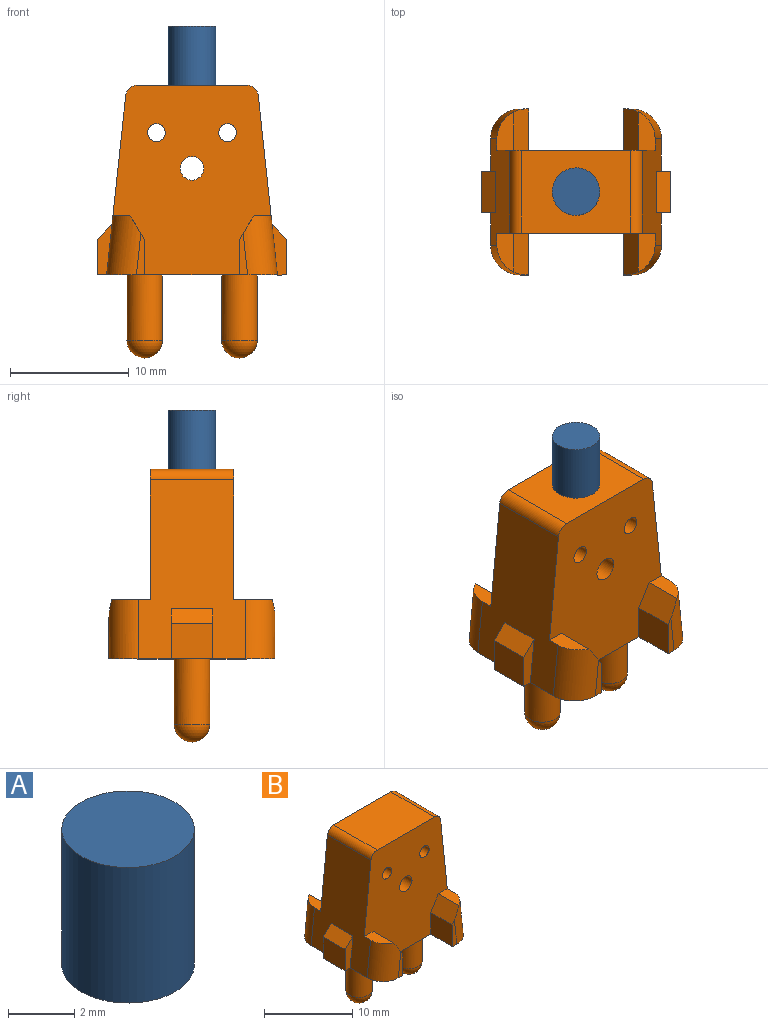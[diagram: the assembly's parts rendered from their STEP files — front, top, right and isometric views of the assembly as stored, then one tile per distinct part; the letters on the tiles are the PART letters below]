
ASSEMBLY  parts=2 mates=1
PART A: 3 faces, bbox 4x4x5 mm
  f0: cylinder r=2mm len=5mm, axis (0,0,-1), area 62.8mm2, adj f1,f2
  f1: plane 4x4mm, normal (0,0,1), area 12.6mm2, adj f0
  f2: plane 4x4mm, normal (0,0,-1), area 12.6mm2, adj f0
PART B: 43 faces, bbox 16x14x23 mm
  f0: plane 15.11x9mm, normal (0.99,0,0.11), area 101.4mm2, adj f1,f7,f9,f10,f22,f24,f32,f34
  f1: cylinder r=1mm len=7mm, axis (0,1,0), area 10.3mm2, adj f0,f2,f9,f10
  f2: plane 9.2x7mm, normal (0,0,1), area 64.4mm2, adj f1,f3,f9,f10
  f3: cylinder r=1mm len=7mm, axis (0,1,0), area 10.3mm2, adj f2,f4,f9,f10
  f4: plane 15.11x9mm, normal (-0.99,0,0.11), area 101.4mm2, adj f3,f7,f9,f10,f17,f19,f27,f29
  f5: cylinder r=1mm len=7mm, axis (0,1,0), area 44mm2, adj f9,f10
  f6: cylinder r=0.75mm len=7mm, axis (0,1,0), area 33mm2, adj f9,f10
  f7: plane 16x14mm, normal (0,0,-1), area 131.7mm2, adj f0,f4,f9,f10,f11,f12,f15,f18
  f8: cylinder r=0.75mm len=7mm, axis (0,1,0), area 33mm2, adj f9,f10
  f9: plane 16x13.34mm, normal (0,-1,0), area 169.3mm2, adj f0,f1,f2,f3,f4,f5,f6,f7
  f10: plane 16x13.34mm, normal (0,1,0), area 169.3mm2, adj f0,f1,f2,f3,f4,f5,f6,f7
  f11: cylinder r=1.5mm len=5.5mm, axis (0,0,1), area 51.8mm2, adj f7,f14
  f12: cylinder r=1.5mm len=5.5mm, axis (0,0,1), area 51.8mm2, adj f7,f13
  f13: sphere r=1.5mm, area 14.1mm2, adj f12
  f14: sphere r=1.5mm, area 14.1mm2, adj f11
  f15: plane 3.5x3mm, normal (1,0,0), area 10.5mm2, adj f7,f9,f16,f18
  f16: plane 3.5x2mm, normal (0.85,0,0.52), area 8.1mm2, adj f9,f15,f17,f18,f19
  f17: plane 3.26x1.44mm, normal (0,0,1), area 3.8mm2, adj f4,f9,f16,f19
  f18: plane 3.51x0.69mm, normal (0,-1,0), area 1.7mm2, adj f7,f15,f16,f19
  f19: cylinder r=2.5mm len=5.42mm, axis (0.11,0,0.99), area 18.9mm2, adj f4,f7,f16,f17,f18
  f20: plane 3.5x2mm, normal (-0.85,0,0.52), area 8.1mm2, adj f9,f21,f22,f23,f24
  f21: plane 3.5x3mm, normal (-1,0,0), area 10.5mm2, adj f7,f9,f20,f23
  f22: plane 3.26x1.44mm, normal (0,0,1), area 3.8mm2, adj f0,f9,f20,f24
  f23: plane 3.51x0.69mm, normal (0,-1,0), area 1.7mm2, adj f7,f20,f21,f24
  f24: cylinder r=2.5mm len=5.42mm, axis (0.11,0,-0.99), area 18.9mm2, adj f0,f7,f20,f22,f23
  f25: plane 3.5x3mm, normal (1,0,0), area 10.5mm2, adj f7,f10,f26,f28
  f26: plane 3.5x2mm, normal (0.85,0,0.52), area 8.1mm2, adj f10,f25,f27,f28,f29
  f27: plane 3.26x1.44mm, normal (0,0,1), area 3.8mm2, adj f4,f10,f26,f29
  f28: plane 3.51x0.69mm, normal (0,1,0), area 1.7mm2, adj f7,f25,f26,f29
  f29: cylinder r=2.5mm len=5.42mm, axis (0.11,0,0.99), area 18.9mm2, adj f4,f7,f26,f27,f28
  f30: plane 3.5x2mm, normal (-0.85,0,0.52), area 8.1mm2, adj f10,f31,f32,f33,f34
  f31: plane 3.5x3mm, normal (-1,0,0), area 10.5mm2, adj f7,f10,f30,f33
  f32: plane 3.26x1.44mm, normal (0,0,1), area 3.8mm2, adj f0,f10,f30,f34
  f33: plane 3.51x0.69mm, normal (0,1,0), area 1.7mm2, adj f7,f30,f31,f34
  f34: cylinder r=2.5mm len=5.42mm, axis (0.11,0,-0.99), area 18.9mm2, adj f0,f7,f30,f32,f33
  f35: plane 3.5x1.25mm, normal (0.71,0,0.71), area 6.2mm2, adj f0,f36,f37,f38
  f36: plane 4.25x1.25mm, normal (0,-1,0), area 3.6mm2, adj f0,f7,f35,f38
  f37: plane 4.25x1.25mm, normal (0,1,0), area 3.6mm2, adj f0,f7,f35,f38
  f38: plane 3.5x3mm, normal (1,0,0), area 10.5mm2, adj f7,f35,f36,f37
  f39: plane 3.5x3mm, normal (-1,0,0), area 10.5mm2, adj f7,f40,f41,f42
  f40: plane 3.5x1.25mm, normal (-0.71,0,0.71), area 6.2mm2, adj f4,f39,f41,f42
  f41: plane 4.25x1.25mm, normal (0,-1,0), area 3.6mm2, adj f4,f7,f39,f40
  f42: plane 4.25x1.25mm, normal (0,1,0), area 3.6mm2, adj f4,f7,f39,f40
PLACE A t=(-2.71,0.03,-2.12)mm
PLACE B t=(-2.71,0.03,-2.12)mm fixed
MATE slider A.f0 <-> B.f2  axis (0,0,-1) through (-2.71,0.03,13.88)mm
